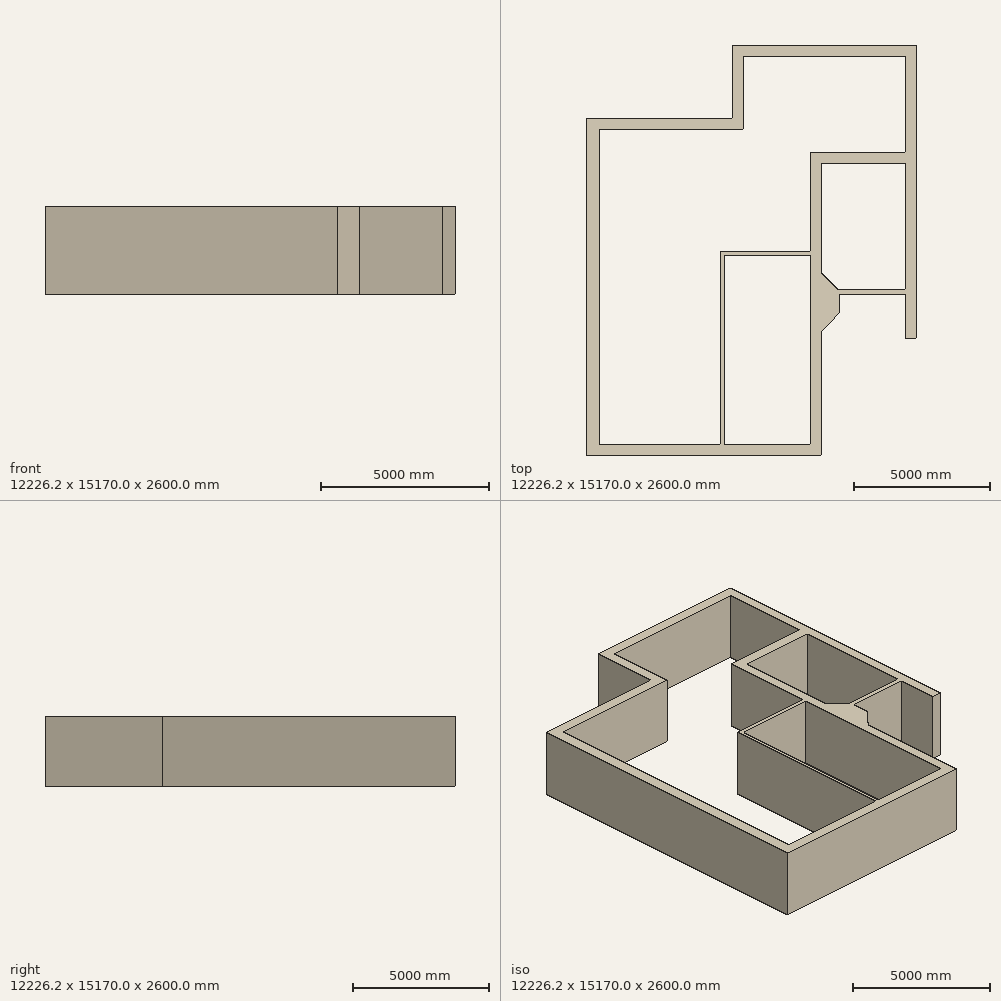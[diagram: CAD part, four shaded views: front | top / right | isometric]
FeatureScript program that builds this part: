
annotation { "Feature Type Name" : "Feature", "Feature Type Description" : "" }
export const myFeature = defineFeature(function(context is Context, id is Id, definition is map)
    precondition{}
    {
        {
            var Q0;
            Q0=qCreatedBy(makeId("Top.planeOp"),FACE);
            var sketch = newSketch(context, id + "F0", { "sketchPlane" : qUnion([Q0])});
            skLineSegment(sketch, "E0.bottom", {"start": v(-6471.68, -10556.28) * mm, "end": v(2238.32, -10556.28) * mm});
            skLineSegment(sketch, "E0.top", {"start": v(-6471.68, 1903.72) * mm, "end": v(-1065.44, 1903.72) * mm});
            skLineSegment(sketch, "E0.left", {"start": v(-6471.68, -10556.28) * mm, "end": v(-6471.68, 1903.72) * mm});
            skLineSegment(sketch, "E0.right", {"start": v(2238.32, -10556.28) * mm, "end": v(2238.32, -5995.48) * mm});
            skLineSegment(sketch, "E1.bottom", {"start": v(5754.56, 4613.72) * mm, "end": v(-1065.44, 4613.72) * mm});
            skLineSegment(sketch, "E1.top", {"start": v(5754.56, 262.9) * mm, "end": v(2238.32, 262.9) * mm});
            skLineSegment(sketch, "E1.left", {"start": v(5754.56, 4613.72) * mm, "end": v(5754.56, 262.9) * mm});
            skLineSegment(sketch, "E1.right", {"start": v(-1065.44, 4613.72) * mm, "end": v(-1065.44, 1903.72) * mm});
            skLineSegment(sketch, "E2.bottom", {"start": v(5754.56, -6226.28) * mm, "end": v(5354.56, -6226.28) * mm});
            skLineSegment(sketch, "E2.top", {"start": v(5754.56, 262.9) * mm, "end": v(5354.56, 262.9) * mm});
            skLineSegment(sketch, "E2.left", {"start": v(5754.56, -6226.28) * mm, "end": v(5754.56, 262.9) * mm});
            skLineSegment(sketch, "E2.right", {"start": v(5354.56, -6226.28) * mm, "end": v(5354.56, -4602.67) * mm});
            skLineSegment(sketch, "E3.bottom", {"start": v(-5996.75, 1503.72) * mm, "end": v(-647.47, 1503.72) * mm});
            skLineSegment(sketch, "E3.top", {"start": v(-5996.75, -10156.28) * mm, "end": v(-1514.27, -10156.28) * mm});
            skLineSegment(sketch, "E3.left", {"start": v(-5996.75, 1503.72) * mm, "end": v(-5996.75, -10156.28) * mm});
            skLineSegment(sketch, "E3.right", {"start": v(1838.32, 662.9) * mm, "end": v(1838.32, -3025.19) * mm});
            skLineSegment(sketch, "E4.bottom", {"start": v(5354.56, 4213.72) * mm, "end": v(-647.47, 4213.72) * mm});
            skLineSegment(sketch, "E4.top", {"start": v(5354.56, 662.9) * mm, "end": v(1838.32, 662.9) * mm});
            skLineSegment(sketch, "E4.left", {"start": v(5354.56, 4213.72) * mm, "end": v(5354.56, 662.9) * mm});
            skLineSegment(sketch, "E4.right", {"start": v(-647.47, 4213.72) * mm, "end": v(-647.47, 1503.72) * mm});
            skLineSegment(sketch, "E5", {"start": v(2238.32, -3810.87) * mm, "end": v(2859.92, -4421.42) * mm});
            skLineSegment(sketch, "E6", {"start": v(2859.92, -4421.42) * mm, "end": v(5354.56, -4421.42) * mm});
            skLineSegment(sketch, "E7", {"start": v(2238.32, -5995.48) * mm, "end": v(2898.08, -5289.54) * mm});
            skLineSegment(sketch, "E8", {"start": v(2898.08, -5289.54) * mm, "end": v(2898.08, -4602.67) * mm});
            skLineSegment(sketch, "E9", {"start": v(2898.08, -4602.67) * mm, "end": v(5354.56, -4602.67) * mm});
            skLineSegment(sketch, "E10.trimOffspring", {"start": v(2238.32, -3810.87) * mm, "end": v(2238.32, 262.9) * mm});
            skLineSegment(sketch, "E11.trimOffspring", {"start": v(5354.56, -4421.42) * mm, "end": v(5354.56, 262.9) * mm});
            skLineSegment(sketch, "E12", {"start": v(1838.32, -3025.19) * mm, "end": v(-1514.27, -3025.19) * mm});
            skLineSegment(sketch, "E13", {"start": v(-1514.27, -3025.19) * mm, "end": v(-1514.27, -10156.28) * mm});
            skLineSegment(sketch, "E14", {"start": v(-1373.56, -10156.28) * mm, "end": v(-1373.56, -3172) * mm});
            skLineSegment(sketch, "E15", {"start": v(-1373.56, -3172) * mm, "end": v(1838.32, -3172) * mm});
            skLineSegment(sketch, "E16.trimOffspring", {"start": v(-1373.56, -10156.28) * mm, "end": v(1838.32, -10156.28) * mm});
            skLineSegment(sketch, "E17.trimOffspring", {"start": v(1838.32, -3172) * mm, "end": v(1838.32, -10156.28) * mm});
            skSolve(sketch);
        }
        {
            var Q0;
            Q0 = qSketchRegion(id + "F0", true);
            extrude(context, id + "F1", {"entities" : qUnion([Q0]), "depth" : 2600 * mm, "offsetDistance" : 25 * mm});
        }
    });
